# Revit family: RN 23108 Valvola diritta
name_source: partatom
category: Rohrzubehör
units: mm (PartAtom-declared; Revit-internal decimal feet)

## family parameters
Arbeitsebenenbasiert = Nein
Beim Laden mit Abzugskörper schneiden = Nein
Bemaßung runder Anschluss = Durchmesser verwenden
Gemeinsam genutzt = Nein
Immer vertikal = Ja
Teiletyp = Ventil - Zerlegung in

## types (7) — shared parameters
1.010.00.2 Blattnummer der Richtlinie = 17
1.010.00.3 Ausgabedatum (Monat) der Richtlinie = 201601
1.010.00.4 Herstellername = R. Nussbaum AG
1.010.00.5 Revisionsdatum der Datei = 20190528
1.010.00.6 Webadresse des Herstellers = http://www.nussbaum.ch
1.100.00.3 Sortiernummer für Anzeigereihenfolge = 1
1.100.00.4 Produktbezeichnung = Absperrarmaturen
1.960/3L.00.8 Link (URL) = https://www.nussbaum.ch
17.700.00.4 Armaturentyp = 1
17.700.00.7 Maximale Betriebstemperatur TB [°C] = 90
17.700.00.8 Maximaler Betriebsdruck (Arbeitsdruck) ps [1.0 · 105 Pa] = 16
Connector Visibility = Nein
EnclosingSpace Visibility = Nein
Hersteller = R. Nussbauzm AG
URL = https://www.nussbaum.ch

## per-type parameters (varying)
- DN 25: 1.800.00.3 TGA-Nummer=001062???00000000000000000000200700000000000000001???00000; 1.810.00.3 Hersteller-Bestellnummer=23108.23; 1.810.00.4 DATANORM-Nummer=23108.23; 1.810.00.5 StLB-Nummer=726.323; 1.810.00.6 GTIN-Nummer=7612945728784; 17.700.00.30 Produktbeschreibung=23108.23, Geradsitzventil, mit Flanschen, DN=25; 17.700.00.5 Nennweite DN=25; 17.700.00.6 kvs-Wert [m3/h]=10.47; CONNECTOR0_DIAMETER_dX_0r=25 mm  [stored 0.082021 ft]; CONNECTOR0_dX_00=63 mm; CONNECTOR0_dX_01=63 mm; CONNECTOR0_ref_dX=63 mm; CONNECTOR1_DIAMETER_dX_0r=25 mm  [stored 0.082021 ft]; CONNECTOR1_dX_00=63 mm; CONNECTOR1_dX_01=63 mm; CONNECTOR1_ref_dX=63 mm; Modell=23108.23; R. Nussbaum AG 23108.23 de Visibility=Ja; R. Nussbaum AG 23108.24 de Visibility=Nein; R. Nussbaum AG 23108.25 de Visibility=Nein; R. Nussbaum AG 23108.26 de Visibility=Nein; R. Nussbaum AG 23108.27 de Visibility=Nein; R. Nussbaum AG 23108.28 de Visibility=Nein; R. Nussbaum AG 23108.29 de Visibility=Nein; Typenkommentare=Valvola dirittaDN 25
- DN 32: 1.800.00.3 TGA-Nummer=001062???00000000000000000000200700000000000000002???00000; 1.810.00.3 Hersteller-Bestellnummer=23108.24; 1.810.00.4 DATANORM-Nummer=23108.24; 1.810.00.5 StLB-Nummer=726.324; 1.810.00.6 GTIN-Nummer=7612945728791; 17.700.00.30 Produktbeschreibung=23108.24, Geradsitzventil, mit Flanschen, DN=32; 17.700.00.5 Nennweite DN=32; 17.700.00.6 kvs-Wert [m3/h]=19.49; CONNECTOR0_DIAMETER_dX_0r=32 mm; CONNECTOR0_dX_00=66 mm; CONNECTOR0_dX_01=65 mm; CONNECTOR0_ref_dX=66 mm; CONNECTOR1_DIAMETER_dX_0r=32 mm; CONNECTOR1_dX_00=65 mm; CONNECTOR1_dX_01=66 mm; CONNECTOR1_ref_dX=66 mm; Modell=23108.24; R. Nussbaum AG 23108.23 de Visibility=Nein; R. Nussbaum AG 23108.24 de Visibility=Ja; R. Nussbaum AG 23108.25 de Visibility=Nein; R. Nussbaum AG 23108.26 de Visibility=Nein; R. Nussbaum AG 23108.27 de Visibility=Nein; R. Nussbaum AG 23108.28 de Visibility=Nein; R. Nussbaum AG 23108.29 de Visibility=Nein; Typenkommentare=Valvola dirittaDN 32
- DN 40: 1.800.00.3 TGA-Nummer=001062???00000000000000000000200700000000000000003???00000; 1.810.00.3 Hersteller-Bestellnummer=23108.25; 1.810.00.4 DATANORM-Nummer=23108.25; 1.810.00.5 StLB-Nummer=726.325; 1.810.00.6 GTIN-Nummer=7612945726827; 17.700.00.30 Produktbeschreibung=23108.25, Geradsitzventil, mit Flanschen, DN=40; 17.700.00.5 Nennweite DN=40; 17.700.00.6 kvs-Wert [m3/h]=24.19; CONNECTOR0_DIAMETER_dX_0r=40 mm; CONNECTOR0_dX_00=71 mm; CONNECTOR0_dX_01=70 mm; CONNECTOR0_ref_dX=71 mm; CONNECTOR1_DIAMETER_dX_0r=40 mm; CONNECTOR1_dX_00=70 mm; CONNECTOR1_dX_01=71 mm; CONNECTOR1_ref_dX=71 mm; Modell=23108.25; R. Nussbaum AG 23108.23 de Visibility=Nein; R. Nussbaum AG 23108.24 de Visibility=Nein; R. Nussbaum AG 23108.25 de Visibility=Ja; R. Nussbaum AG 23108.26 de Visibility=Nein; R. Nussbaum AG 23108.27 de Visibility=Nein; R. Nussbaum AG 23108.28 de Visibility=Nein; R. Nussbaum AG 23108.29 de Visibility=Nein; Typenkommentare=Valvola dirittaDN 40
- DN 50: 1.800.00.3 TGA-Nummer=001062???00000000000000000000200700000000000000004???00000; 1.810.00.3 Hersteller-Bestellnummer=23108.26; 1.810.00.4 DATANORM-Nummer=23108.26; 1.810.00.5 StLB-Nummer=726.326; 1.810.00.6 GTIN-Nummer=7612945726834; 17.700.00.30 Produktbeschreibung=23108.26, Geradsitzventil, mit Flanschen, DN=50; 17.700.00.5 Nennweite DN=50; 17.700.00.6 kvs-Wert [m3/h]=38.33; CONNECTOR0_DIAMETER_dX_0r=50 mm; CONNECTOR0_dX_00=76 mm; CONNECTOR0_dX_01=75 mm  [stored 0.246063 ft]; CONNECTOR0_ref_dX=76 mm; CONNECTOR1_DIAMETER_dX_0r=50 mm; CONNECTOR1_dX_00=75 mm  [stored 0.246063 ft]; CONNECTOR1_dX_01=76 mm; CONNECTOR1_ref_dX=76 mm; Modell=23108.26; R. Nussbaum AG 23108.23 de Visibility=Nein; R. Nussbaum AG 23108.24 de Visibility=Nein; R. Nussbaum AG 23108.25 de Visibility=Nein; R. Nussbaum AG 23108.26 de Visibility=Ja; R. Nussbaum AG 23108.27 de Visibility=Nein; R. Nussbaum AG 23108.28 de Visibility=Nein; R. Nussbaum AG 23108.29 de Visibility=Nein; Typenkommentare=Valvola dirittaDN 50
- DN 65: 1.800.00.3 TGA-Nummer=001062???00000000000000000000200700000000000000005???00000; 1.810.00.3 Hersteller-Bestellnummer=23108.27; 1.810.00.4 DATANORM-Nummer=23108.27; 1.810.00.5 StLB-Nummer=726.327; 1.810.00.6 GTIN-Nummer=7612945726209; 17.700.00.30 Produktbeschreibung=23108.27, Geradsitzventil, mit Flanschen, DN=65; 17.700.00.5 Nennweite DN=65; 17.700.00.6 kvs-Wert [m3/h]=65.27; CONNECTOR0_DIAMETER_dX_0r=65 mm; CONNECTOR0_dX_00=85 mm; CONNECTOR0_dX_01=65 mm; CONNECTOR0_ref_dX=65 mm; CONNECTOR1_DIAMETER_dX_0r=65 mm; CONNECTOR1_dX_00=65 mm; CONNECTOR1_dX_01=85 mm; CONNECTOR1_ref_dX=65 mm; Modell=23108.27; R. Nussbaum AG 23108.23 de Visibility=Nein; R. Nussbaum AG 23108.24 de Visibility=Nein; R. Nussbaum AG 23108.25 de Visibility=Nein; R. Nussbaum AG 23108.26 de Visibility=Nein; R. Nussbaum AG 23108.27 de Visibility=Ja; R. Nussbaum AG 23108.28 de Visibility=Nein; R. Nussbaum AG 23108.29 de Visibility=Nein; Typenkommentare=Valvola dirittaDN 65
- DN 80: 1.800.00.3 TGA-Nummer=001062???00000000000000000000200700000000000000006???00000; 1.810.00.3 Hersteller-Bestellnummer=23108.28; 1.810.00.4 DATANORM-Nummer=23108.28; 1.810.00.5 StLB-Nummer=726.328; 1.810.00.6 GTIN-Nummer=7612945726285; 17.700.00.30 Produktbeschreibung=23108.28, Geradsitzventil, mit Flanschen, DN=80; 17.700.00.5 Nennweite DN=80; 17.700.00.6 kvs-Wert [m3/h]=93.54; CONNECTOR0_DIAMETER_dX_0r=80 mm; CONNECTOR0_dX_00=90 mm; CONNECTOR0_dX_01=70 mm; CONNECTOR0_ref_dX=70 mm; CONNECTOR1_DIAMETER_dX_0r=80 mm; CONNECTOR1_dX_00=70 mm; CONNECTOR1_dX_01=90 mm; CONNECTOR1_ref_dX=70 mm; Modell=23108.28; R. Nussbaum AG 23108.23 de Visibility=Nein; R. Nussbaum AG 23108.24 de Visibility=Nein; R. Nussbaum AG 23108.25 de Visibility=Nein; R. Nussbaum AG 23108.26 de Visibility=Nein; R. Nussbaum AG 23108.27 de Visibility=Nein; R. Nussbaum AG 23108.28 de Visibility=Ja; R. Nussbaum AG 23108.29 de Visibility=Nein; Typenkommentare=Valvola dirittaDN 80
- DN 100: 1.800.00.3 TGA-Nummer=001062???00000000000000000000200700000000000000007???00000; 1.810.00.3 Hersteller-Bestellnummer=23108.29; 1.810.00.4 DATANORM-Nummer=23108.29; 1.810.00.5 StLB-Nummer=726.321; 1.810.00.6 GTIN-Nummer=7612945726292; 17.700.00.30 Produktbeschreibung=23108.29, Geradsitzventil, mit Flanschen, DN=100; 17.700.00.5 Nennweite DN=100; 17.700.00.6 kvs-Wert [m3/h]=152.92; CONNECTOR0_DIAMETER_dX_0r=100 mm  [stored 0.328084 ft]; CONNECTOR0_dX_00=95 mm; CONNECTOR0_dX_01=75 mm  [stored 0.246063 ft]; CONNECTOR0_ref_dX=75 mm  [stored 0.246063 ft]; CONNECTOR1_DIAMETER_dX_0r=100 mm  [stored 0.328084 ft]; CONNECTOR1_dX_00=75 mm  [stored 0.246063 ft]; CONNECTOR1_dX_01=95 mm; CONNECTOR1_ref_dX=75 mm  [stored 0.246063 ft]; Modell=23108.29; R. Nussbaum AG 23108.23 de Visibility=Nein; R. Nussbaum AG 23108.24 de Visibility=Nein; R. Nussbaum AG 23108.25 de Visibility=Nein; R. Nussbaum AG 23108.26 de Visibility=Nein; R. Nussbaum AG 23108.27 de Visibility=Nein; R. Nussbaum AG 23108.28 de Visibility=Nein; R. Nussbaum AG 23108.29 de Visibility=Ja; Typenkommentare=Valvola dirittaDN 100

note: [stored X ft] marks values corroborated as IEEE doubles in the binary element streams (Revit-internal decimal feet)

## geometry (parser evidence)
native form markers: Sweep x1
no freeform markers — native parametric forms only
